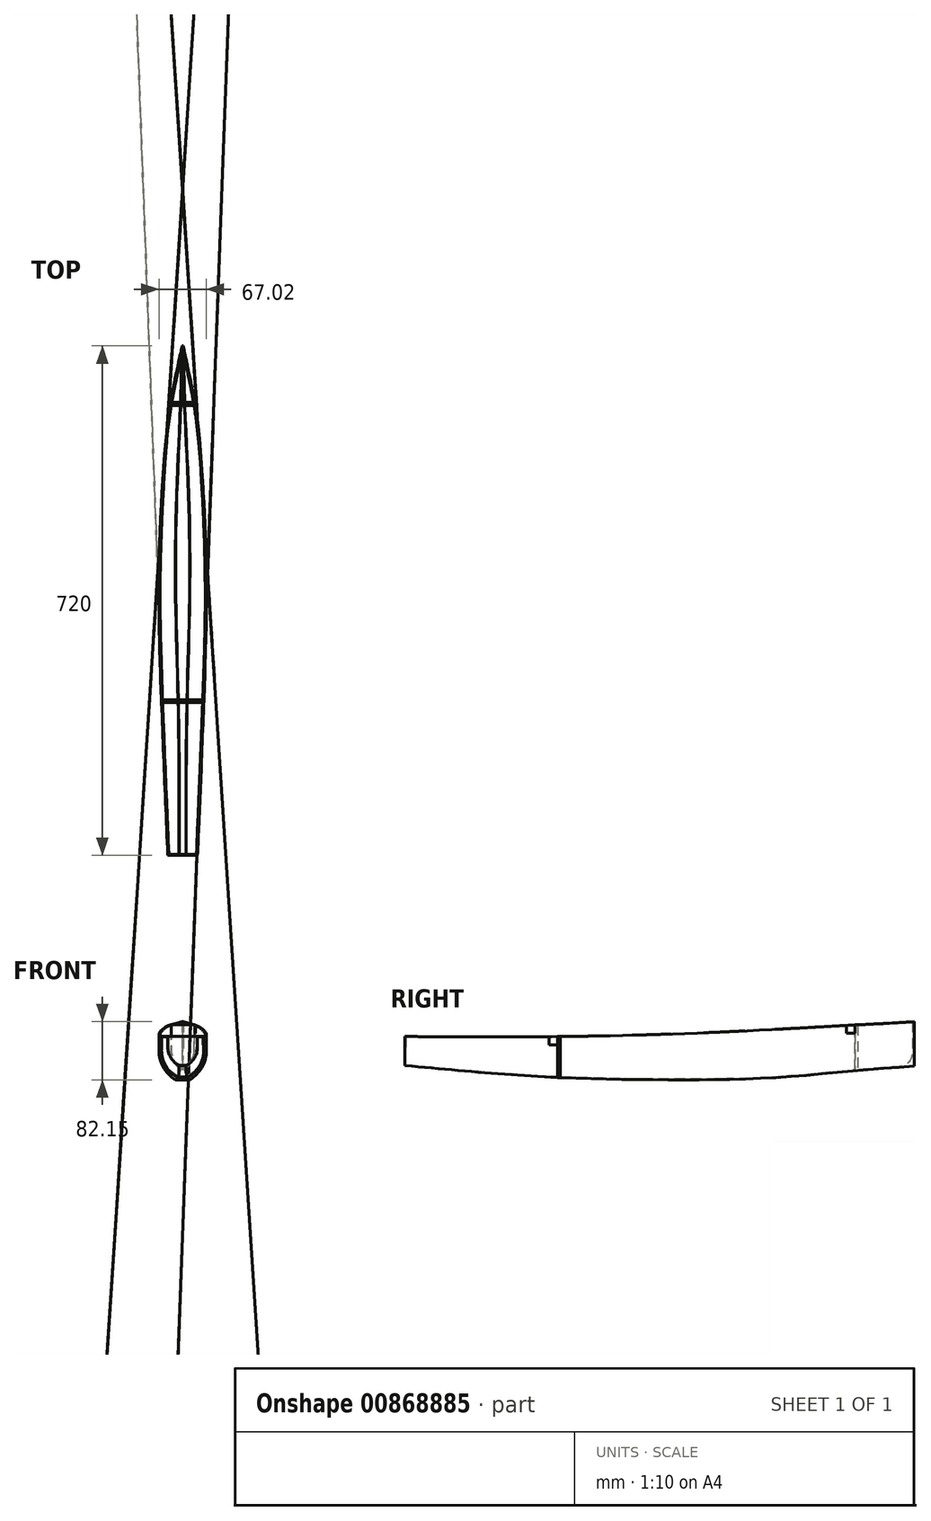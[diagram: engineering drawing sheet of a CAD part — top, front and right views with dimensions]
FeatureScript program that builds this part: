
annotation { "Feature Type Name" : "Feature", "Feature Type Description" : "" }
export const myFeature = defineFeature(function(context is Context, id is Id, definition is map)
    precondition{}
    {
        {
            var Q0;
            Q0=qCreatedBy(makeId("Front.planeOp"),FACE);
            var sketch = newSketch(context, id + "F0", { "sketchPlane" : qUnion([Q0])});
            skLineSegment(sketch, "E0", {"start": v(0, 20) * mm, "end": v(0, 61) * mm, "construction": true});
            skLineSegment(sketch, "E1", {"start": v(0, 61) * mm, "end": v(21, 61) * mm});
            skLineSegment(sketch, "E2", {"start": v(21, 61) * mm, "end": v(21, 46) * mm});
            skLineSegment(sketch, "E3", {"start": v(0, 20) * mm, "end": v(5, 20) * mm});
            skArc(sketch, "E4", {"start": v(5, 20) * mm, "mid": v(16.68, 30.74) * mm, "end": v(21, 46) * mm});
            skPoint(sketch, "E4.third.point", {"position": v(-37.23, 47) * mm});
            skLineSegment(sketch, "E5.MirrorCS", {"start": v(0, 61) * mm, "end": v(-21, 61) * mm});
            skLineSegment(sketch, "E6.MirrorCS", {"start": v(-21, 61) * mm, "end": v(-21, 46) * mm});
            skArc(sketch, "E7.MirrorCS", {"start": v(-5, 20) * mm, "mid": v(-16.68, 30.74) * mm, "end": v(-21, 46) * mm});
            skLineSegment(sketch, "E8.MirrorCS", {"start": v(0, 20) * mm, "end": v(-5, 20) * mm});
            skLineSegment(sketch, "E9", {"start": v(-75.3, 0) * mm, "end": v(75.14, 0) * mm, "construction": true});
            skSolve(sketch);
        }
        {
            var Q0;
            Q0=qCreatedBy(makeId("Front.planeOp"),FACE);
            cPlane(context, id + "F1", {"entities" : qUnion([Q0]), "cplaneType" : CPlaneType.OFFSET, "offset" : 360 * mm, "oppositeDirection" : true, "width" : 150 * mm, "height" : 150 * mm});
        }
        {
            var Q0;
            Q0=qCreatedBy(id+"F1.planeOp",FACE);
            var sketch = newSketch(context, id + "F2", { "sketchPlane" : qUnion([Q0])});
            skLineSegment(sketch, "E10", {"start": v(-102.94, 0) * mm, "end": v(102.49, 0) * mm, "construction": true});
            skLineSegment(sketch, "E11", {"start": v(10, 0) * mm, "end": v(0, 0) * mm});
            skLineSegment(sketch, "E12", {"start": v(0, 0) * mm, "end": v(0, 64) * mm, "construction": true});
            skLineSegment(sketch, "E13", {"start": v(0, 64) * mm, "end": v(33.5, 64) * mm});
            skLineSegment(sketch, "E14", {"start": v(33.5, 64) * mm, "end": v(33.5, 39) * mm});
            skPoint(sketch, "E15.third.point", {"position": v(-30.1, 50.85) * mm});
            skPoint(sketch, "E16.third.point", {"position": v(-60.87, 30.93) * mm});
            skArc(sketch, "E17.trimOffspring", {"start": v(10, 0) * mm, "mid": v(26.73, 16.5) * mm, "end": v(33.5, 39) * mm});
            skLineSegment(sketch, "E18.MirrorCS", {"start": v(0, 64) * mm, "end": v(-33.5, 64) * mm});
            skLineSegment(sketch, "E19.MirrorCS", {"start": v(-33.5, 64) * mm, "end": v(-33.5, 39) * mm});
            skArc(sketch, "E20.MirrorCS", {"start": v(-10, 0) * mm, "mid": v(-26.73, 16.5) * mm, "end": v(-33.5, 39) * mm});
            skLineSegment(sketch, "E21.MirrorCS", {"start": v(-10, 0) * mm, "end": v(0, 0) * mm});
            skSolve(sketch);
        }
        {
            var Q0;
            Q0=qCreatedBy(makeId("Front.planeOp"),FACE);
            cPlane(context, id + "F3", {"entities" : qUnion([Q0]), "cplaneType" : CPlaneType.OFFSET, "offset" : 540 * mm, "oppositeDirection" : true, "width" : 150 * mm, "height" : 150 * mm});
        }
        {
            var Q0;
            Q0=qCreatedBy(id+"F3.planeOp",FACE);
            var sketch = newSketch(context, id + "F4", { "sketchPlane" : qUnion([Q0])});
            skLineSegment(sketch, "E22", {"start": v(-37.15, 0) * mm, "end": v(37.58, 0) * mm, "construction": true});
            skLineSegment(sketch, "E23", {"start": v(7.5, 4) * mm, "end": v(0, 4) * mm});
            skLineSegment(sketch, "E24", {"start": v(0, 4) * mm, "end": v(0, 72) * mm, "construction": true});
            skLineSegment(sketch, "E25", {"start": v(0, 72) * mm, "end": v(27.5, 72) * mm});
            skLineSegment(sketch, "E26", {"start": v(27.5, 72) * mm, "end": v(27.5, 42) * mm});
            skArc(sketch, "E27", {"start": v(7.5, 4) * mm, "mid": v(22.2, 20.53) * mm, "end": v(27.5, 42) * mm});
            skPoint(sketch, "E27.third.point", {"position": v(-63.9, 33.44) * mm});
            skLineSegment(sketch, "E28.MirrorCS", {"start": v(0, 72) * mm, "end": v(-27.5, 72) * mm});
            skLineSegment(sketch, "E29.MirrorCS", {"start": v(-27.5, 72) * mm, "end": v(-27.5, 42) * mm});
            skArc(sketch, "E30.MirrorCS", {"start": v(-7.5, 4) * mm, "mid": v(-22.2, 20.53) * mm, "end": v(-27.5, 42) * mm});
            skLineSegment(sketch, "E31.MirrorCS", {"start": v(-7.5, 4) * mm, "end": v(0, 4) * mm});
            skSolve(sketch);
        }
        {
            var Q0;
            Q0=qCreatedBy(id+"F3.planeOp",FACE);
            cPlane(context, id + "F5", {"entities" : qUnion([Q0]), "cplaneType" : CPlaneType.OFFSET, "offset" : 165 * mm, "oppositeDirection" : true, "width" : 150 * mm, "height" : 150 * mm});
        }
        {
            var Q0;
            Q0=qCreatedBy(id+"F5.planeOp",FACE);
            var sketch = newSketch(context, id + "F6", { "sketchPlane" : qUnion([Q0])});
            skLineSegment(sketch, "E32", {"start": v(1, 18) * mm, "end": v(0, 18) * mm});
            skLineSegment(sketch, "E33", {"start": v(0, 18) * mm, "end": v(0, 81) * mm, "construction": true});
            skLineSegment(sketch, "E34", {"start": v(0, 81) * mm, "end": v(4, 81) * mm});
            skPoint(sketch, "E35.third.point", {"position": v(-87.31, 120.1) * mm});
            skLineSegment(sketch, "E36", {"start": v(4, 81) * mm, "end": v(4, 41) * mm});
            skArc(sketch, "E37", {"start": v(1, 18) * mm, "mid": v(3.25, 29.4) * mm, "end": v(4, 41) * mm});
            skPoint(sketch, "E37.third.point", {"position": v(-168.68, 74.9) * mm});
            skLineSegment(sketch, "E38.MirrorCS", {"start": v(0, 81) * mm, "end": v(-4, 81) * mm});
            skLineSegment(sketch, "E39.MirrorCS", {"start": v(-4, 81) * mm, "end": v(-4, 41) * mm});
            skArc(sketch, "E40.MirrorCS", {"start": v(-1, 18) * mm, "mid": v(-3.25, 29.4) * mm, "end": v(-4, 41) * mm});
            skLineSegment(sketch, "E41.MirrorCS", {"start": v(-1, 18) * mm, "end": v(0, 18) * mm});
            skSolve(sketch);
        }
        {
            var Q0;
            Q0=qCreatedBy(id+"F5.planeOp",FACE);
            cPlane(context, id + "F7", {"entities" : qUnion([Q0]), "cplaneType" : CPlaneType.OFFSET, "offset" : 15 * mm, "oppositeDirection" : true, "width" : 150 * mm, "height" : 150 * mm});
        }
        {
            var Q0;
            Q0=qCreatedBy(id+"F7.planeOp",FACE);
            var sketch = newSketch(context, id + "F8", { "sketchPlane" : qUnion([Q0])});
            skLineSegment(sketch, "E42", {"start": v(0.25, 19) * mm, "end": v(0, 19) * mm});
            skLineSegment(sketch, "E43", {"start": v(0, 19) * mm, "end": v(0, 82) * mm, "construction": true});
            skLineSegment(sketch, "E44", {"start": v(0, 82) * mm, "end": v(1, 82) * mm});
            skLineSegment(sketch, "E45", {"start": v(1, 82) * mm, "end": v(1, 42) * mm});
            skArc(sketch, "E46", {"start": v(0.25, 19) * mm, "mid": v(0.81, 30.5) * mm, "end": v(1, 42) * mm});
            skPoint(sketch, "E46.third.point", {"position": v(-504.86, 360.25) * mm});
            skLineSegment(sketch, "E47.MirrorCS", {"start": v(0, 82) * mm, "end": v(-1, 82) * mm});
            skLineSegment(sketch, "E48.MirrorCS", {"start": v(-1, 82) * mm, "end": v(-1, 42) * mm});
            skArc(sketch, "E49.MirrorCS", {"start": v(-0.25, 19) * mm, "mid": v(-0.81, 30.5) * mm, "end": v(-1, 42) * mm});
            skLineSegment(sketch, "E50.MirrorCS", {"start": v(-0.25, 19) * mm, "end": v(0, 19) * mm});
            skSolve(sketch);
        }
        {
            var Q0;
            Q0=qCreatedBy(makeId("Front.planeOp"),FACE);
            cPlane(context, id + "F9", {"entities" : qUnion([Q0]), "cplaneType" : CPlaneType.OFFSET, "offset" : 220 * mm, "oppositeDirection" : true, "width" : 150 * mm, "height" : 150 * mm});
        }
        {
            var Q0;
            Q0=qCreatedBy(id+"F9.planeOp",FACE);
            var sketch = newSketch(context, id + "F10", { "sketchPlane" : qUnion([Q0])});
            skLineSegment(sketch, "E51", {"start": v(6.5, 3) * mm, "end": v(0, 3) * mm});
            skLineSegment(sketch, "E52", {"start": v(0, 3) * mm, "end": v(0, 61) * mm, "construction": true});
            skLineSegment(sketch, "E53", {"start": v(0, 61) * mm, "end": v(30, 61) * mm});
            skLineSegment(sketch, "E54", {"start": v(30, 61) * mm, "end": v(30, 41) * mm});
            skArc(sketch, "E55", {"start": v(6.5, 3) * mm, "mid": v(23.65, 18.66) * mm, "end": v(30, 41) * mm});
            skPoint(sketch, "E55.third.point", {"position": v(-48.56, 63.4) * mm});
            skLineSegment(sketch, "E56.MirrorCS", {"start": v(0, 61) * mm, "end": v(-30, 61) * mm});
            skLineSegment(sketch, "E57.MirrorCS", {"start": v(-30, 61) * mm, "end": v(-30, 41) * mm});
            skArc(sketch, "E58.MirrorCS", {"start": v(-6.5, 3) * mm, "mid": v(-23.65, 18.66) * mm, "end": v(-30, 41) * mm});
            skLineSegment(sketch, "E59.MirrorCS", {"start": v(-6.5, 3) * mm, "end": v(0, 3) * mm});
            skSolve(sketch);
        }
        {
            var Q0;
            Q0=qCreatedBy(id+"F3.planeOp",FACE);
            cPlane(context, id + "F11", {"entities" : qUnion([Q0]), "cplaneType" : CPlaneType.OFFSET, "offset" : 100 * mm, "oppositeDirection" : true, "width" : 150 * mm, "height" : 150 * mm});
        }
        {
            var Q0;
            Q0=qCreatedBy(id+"F11.planeOp",FACE);
            var sketch = newSketch(context, id + "F12", { "sketchPlane" : qUnion([Q0])});
            skLineSegment(sketch, "E60", {"start": v(3, 13) * mm, "end": v(0, 13) * mm});
            skLineSegment(sketch, "E61", {"start": v(0, 13) * mm, "end": v(0, 77.5) * mm, "construction": true});
            skLineSegment(sketch, "E62", {"start": v(0, 77.5) * mm, "end": v(17, 77.5) * mm});
            skLineSegment(sketch, "E63", {"start": v(17, 77.5) * mm, "end": v(17, 42.5) * mm});
            skArc(sketch, "E64", {"start": v(3, 13) * mm, "mid": v(13.32, 26.17) * mm, "end": v(17, 42.5) * mm});
            skPoint(sketch, "E64.third.point", {"position": v(-59.12, 44.16) * mm});
            skLineSegment(sketch, "E65.MirrorCS", {"start": v(-3, 13) * mm, "end": v(0, 13) * mm});
            skArc(sketch, "E66.MirrorCS", {"start": v(-3, 13) * mm, "mid": v(-13.32, 26.17) * mm, "end": v(-17, 42.5) * mm});
            skLineSegment(sketch, "E67.MirrorCS", {"start": v(-17, 77.5) * mm, "end": v(-17, 42.5) * mm});
            skLineSegment(sketch, "E68.MirrorCS", {"start": v(0, 77.5) * mm, "end": v(-17, 77.5) * mm});
            skSolve(sketch);
        }
        {
            var Q0;
            Q0=makeQuery(id+"F0.imprint","IMPRINT",FACE,{"disambiguationData":[TD([[makeQuery(id+"F0.imprint","IMPRINT",EDGE,{"derivedFrom":sQuery(id+"F0.wireOp",EDGE,"E1")}),-1.0]])]});
            var Q1;
            Q1=makeQuery(id+"F10.imprint","IMPRINT",FACE,{"disambiguationData":[TD([[makeQuery(id+"F10.imprint","IMPRINT",EDGE,{"derivedFrom":sQuery(id+"F10.wireOp",EDGE,"E51")}),-1.0]])]});
            var Q2;
            Q2=makeQuery(id+"F2.imprint","IMPRINT",FACE,{"disambiguationData":[TD([[makeQuery(id+"F2.imprint","IMPRINT",EDGE,{"derivedFrom":sQuery(id+"F2.wireOp",EDGE,"E11")}),-1.0]])]});
            var Q3;
            Q3=makeQuery(id+"F4.imprint","IMPRINT",FACE,{"disambiguationData":[TD([[makeQuery(id+"F4.imprint","IMPRINT",EDGE,{"derivedFrom":sQuery(id+"F4.wireOp",EDGE,"E23")}),-1.0]])]});
            var Q4;
            Q4=makeQuery(id+"F12.imprint","IMPRINT",FACE,{"disambiguationData":[TD([[makeQuery(id+"F12.imprint","IMPRINT",EDGE,{"derivedFrom":sQuery(id+"F12.wireOp",EDGE,"E60")}),-1.0]])]});
            var Q5;
            Q5=makeQuery(id+"F6.imprint","IMPRINT",FACE,{"disambiguationData":[TD([[makeQuery(id+"F6.imprint","IMPRINT",EDGE,{"derivedFrom":sQuery(id+"F6.wireOp",EDGE,"E32")}),-1.0]])]});
            var Q6;
            Q6=makeQuery(id+"F8.imprint","IMPRINT",FACE,{"disambiguationData":[TD([[makeQuery(id+"F8.imprint","IMPRINT",EDGE,{"derivedFrom":sQuery(id+"F8.wireOp",EDGE,"E42")}),-1.0]])]});
            loft(context, id + "F13", {"sheetProfilesArray" : [{ "sheetProfileEntities" : qUnion([Q0]) }, { "sheetProfileEntities" : qUnion([Q1]) }, { "sheetProfileEntities" : qUnion([Q2]) }, { "sheetProfileEntities" : qUnion([Q3]) }, { "sheetProfileEntities" : qUnion([Q4]) }, { "sheetProfileEntities" : qUnion([Q5]) }, { "sheetProfileEntities" : qUnion([Q6]) }]});
        }
        {
            var Q0;
            Q0=makeQuery(id+"F13.opLoft","SWEPT_FACE",FACE,{"disambiguationData":[OSD([sQuery(id+"F0.wireOp",EDGE,"E1"),sQuery(id+"F0.wireOp",EDGE,"E5.MirrorCS"),sQuery(id+"F0.wireOp",EDGE,"E6.MirrorCS"),sQuery(id+"F2.wireOp",EDGE,"E13"),sQuery(id+"F2.wireOp",EDGE,"E18.MirrorCS"),sQuery(id+"F2.wireOp",EDGE,"E19.MirrorCS"),sQuery(id+"F4.wireOp",EDGE,"E25"),sQuery(id+"F4.wireOp",EDGE,"E28.MirrorCS"),sQuery(id+"F4.wireOp",EDGE,"E29.MirrorCS"),sQuery(id+"F6.wireOp",EDGE,"E34"),sQuery(id+"F6.wireOp",EDGE,"E38.MirrorCS"),sQuery(id+"F6.wireOp",EDGE,"E39.MirrorCS"),sQuery(id+"F8.wireOp",EDGE,"E44"),sQuery(id+"F8.wireOp",EDGE,"E47.MirrorCS"),sQuery(id+"F8.wireOp",EDGE,"E48.MirrorCS"),sQuery(id+"F10.wireOp",EDGE,"E53"),sQuery(id+"F10.wireOp",EDGE,"E56.MirrorCS"),sQuery(id+"F10.wireOp",EDGE,"E57.MirrorCS"),sQuery(id+"F12.wireOp",EDGE,"E62"),sQuery(id+"F12.wireOp",EDGE,"E67.MirrorCS"),sQuery(id+"F12.wireOp",EDGE,"E68.MirrorCS")])]});
            shell(context, id + "F14", {"entities" : qUnion([Q0]), "thickness" : 1.5 * mm});
        }
        {
            var Q0;
            Q0 = qSketchRegion(id + "F12", true);
            extrude(context, id + "F15", {"entities" : qUnion([Q0]), "operationType" : NewBodyOperationType.ADD, "depth" : 4 * mm, "offsetDistance" : 25 * mm});
        }
        {
            var Q0;
            Q0 = qSketchRegion(id + "F10", true);
            extrude(context, id + "F16", {"entities" : qUnion([Q0]), "operationType" : NewBodyOperationType.ADD, "depth" : 4 * mm, "offsetDistance" : 25 * mm});
        }
        {
            var Q0;
            Q0=qCreatedBy(makeId("Right.planeOp"),FACE);
            var sketch = newSketch(context, id + "F17", { "sketchPlane" : qUnion([Q0])});
            skLineSegment(sketch, "E69.bottom", {"start": v(204, 60.96) * mm, "end": v(216, 60.96) * mm});
            skLineSegment(sketch, "E69.top", {"start": v(204, 48.96) * mm, "end": v(216, 48.96) * mm});
            skLineSegment(sketch, "E69.left", {"start": v(204, 60.96) * mm, "end": v(204, 48.96) * mm});
            skLineSegment(sketch, "E69.right", {"start": v(216, 60.96) * mm, "end": v(216, 48.96) * mm});
            skLineSegment(sketch, "E70.bottom", {"start": v(624, 77.5) * mm, "end": v(636, 77.5) * mm});
            skLineSegment(sketch, "E70.top", {"start": v(624, 65.5) * mm, "end": v(636, 65.5) * mm});
            skLineSegment(sketch, "E70.left", {"start": v(624, 77.5) * mm, "end": v(624, 65.5) * mm});
            skLineSegment(sketch, "E70.right", {"start": v(636, 77.5) * mm, "end": v(636, 65.5) * mm});
            skSolve(sketch);
        }
        {
            var Q0;
            Q0=makeQuery(id+"F17.imprint","IMPRINT",FACE,{"disambiguationData":[TD([[makeQuery(id+"F17.imprint","IMPRINT",EDGE,{"derivedFrom":sQuery(id+"F17.wireOp",EDGE,"E69.bottom")}),-1.0]])]});
            var Q1;
            Q1=makeQuery(id+"F17.imprint","IMPRINT",FACE,{"disambiguationData":[TD([[makeQuery(id+"F17.imprint","IMPRINT",EDGE,{"derivedFrom":sQuery(id+"F17.wireOp",EDGE,"E70.bottom")}),-1.0]])]});
            extrude(context, id + "F18", {"entities" : qUnion([Q0, Q1]), "operationType" : NewBodyOperationType.REMOVE, "depth" : 50 * mm, "offsetDistance" : 25 * mm});
        }
    });
